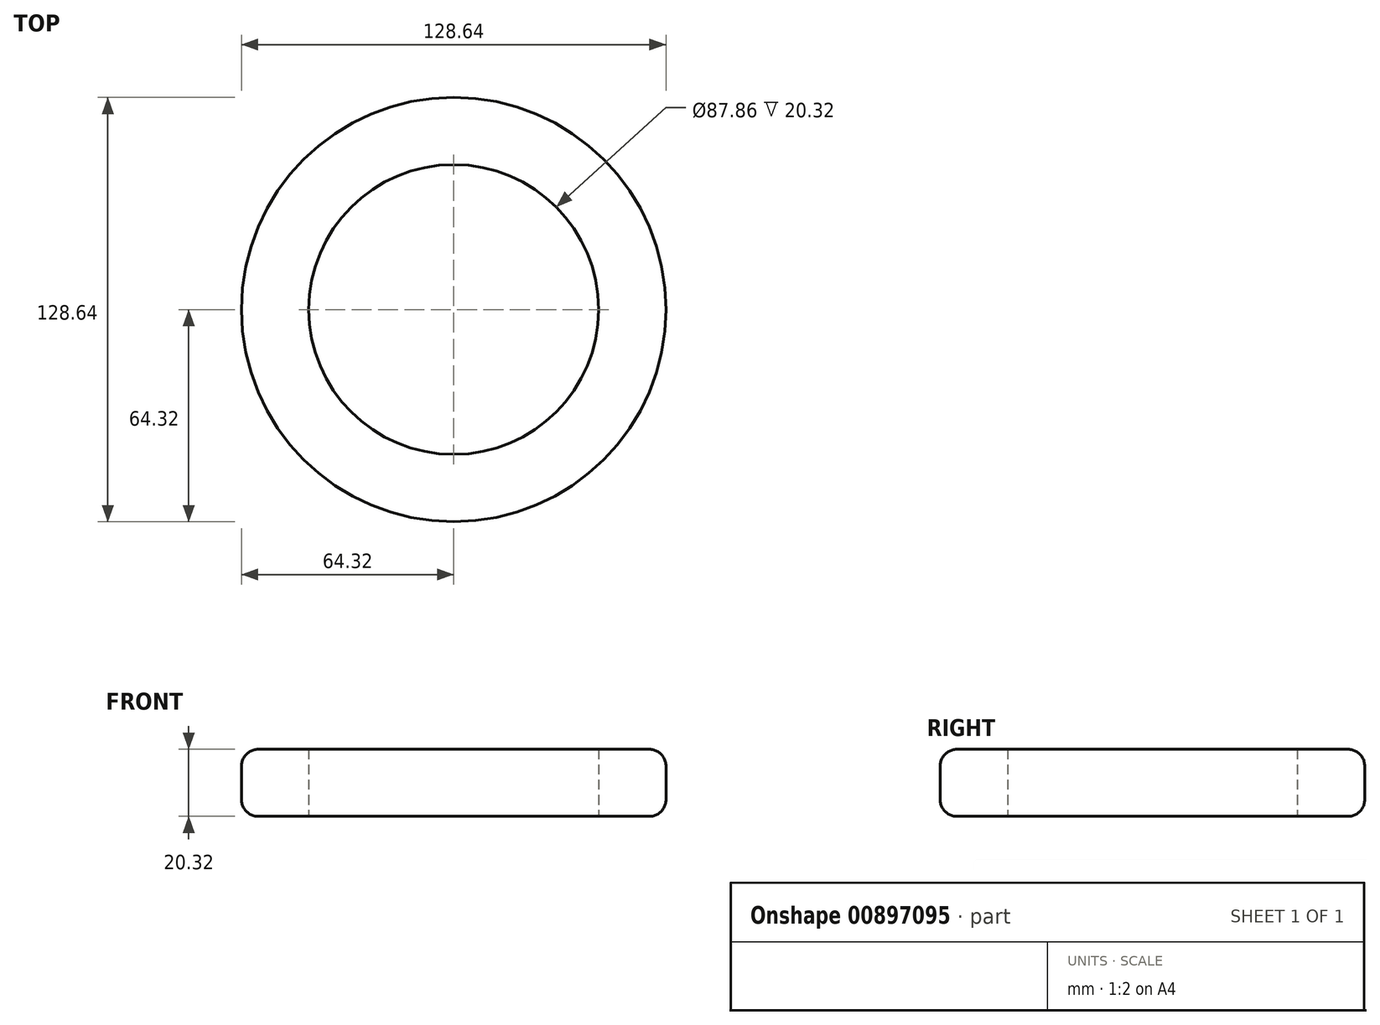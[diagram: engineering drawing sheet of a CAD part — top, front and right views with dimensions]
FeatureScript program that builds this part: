
annotation { "Feature Type Name" : "Feature", "Feature Type Description" : "" }
export const myFeature = defineFeature(function(context is Context, id is Id, definition is map)
    precondition{}
    {
        {
            var Q0;
            Q0=qCreatedBy(makeId("Top.planeOp"),FACE);
            var sketch = newSketch(context, id + "F0", { "sketchPlane" : qUnion([Q0])});
            skCircle(sketch, "E0", {"center": v(0, 0) * mm, "radius": 64.32 * mm});
            skCircle(sketch, "E1", {"center": v(0, 0) * mm, "radius": 43.93 * mm});
            skSolve(sketch);
        }
        {
            var Q0;
            Q0 = qSketchRegion(id + "F0", true);
            extrude(context, id + "F1", {"entities" : qUnion([Q0]), "depth" : 20.32 * mm, "offsetDistance" : 25.4 * mm});
        }
        {
            var Q0;
            Q0=makeQuery(id+"F1.opExtrude","CAP_EDGE",EDGE,{"disambiguationData":[OSD([sQuery(id+"F0.wireOp",EDGE,"E0")])],"isStart":false});
            var Q1;
            Q1=makeQuery(id+"F1.opExtrude","SWEPT_FACE",FACE,{"disambiguationData":[OSD([sQuery(id+"F0.wireOp",EDGE,"E0")])]});
            fillet(context, id + "F2", {"entities" : qUnion([Q0, Q1]), "radius" : 5.08 * mm, "tangentPropagation" : true, "allowEdgeOverflow" : false});
        }
    });
